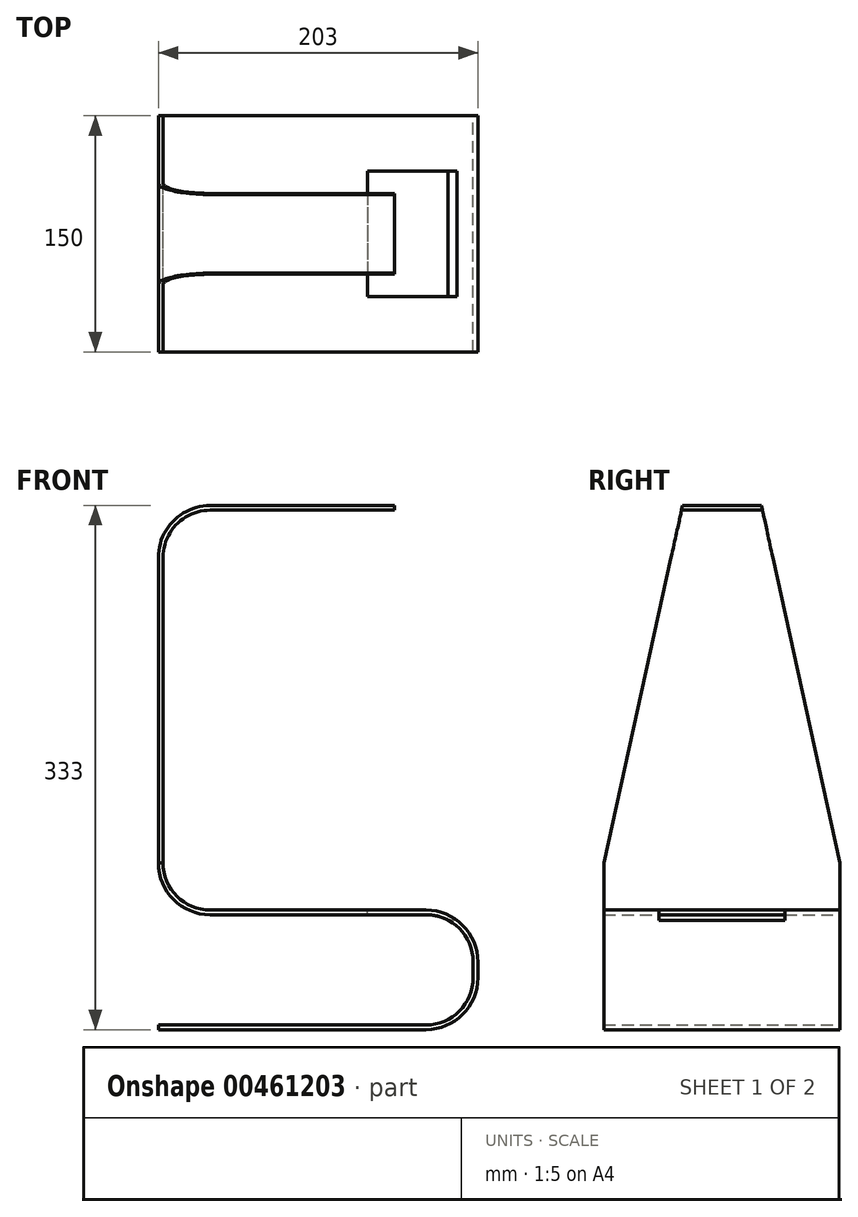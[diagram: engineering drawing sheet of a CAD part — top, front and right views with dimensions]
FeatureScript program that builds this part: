
annotation { "Feature Type Name" : "Feature", "Feature Type Description" : "" }
export const myFeature = defineFeature(function(context is Context, id is Id, definition is map)
    precondition{}
    {
        {
            var Q0;
            Q0=qCreatedBy(makeId("Front.planeOp"),FACE);
            var sketch = newSketch(context, id + "F0", { "sketchPlane" : qUnion([Q0])});
            skLineSegment(sketch, "E0.bottom", {"start": v(70, 35) * mm, "end": v(-67, 35) * mm});
            skLineSegment(sketch, "E0.top", {"start": v(70, -35) * mm, "end": v(-100, -35) * mm});
            skLineSegment(sketch, "E0.left", {"start": v(100, 5) * mm, "end": v(100, -5) * mm});
            skPoint(sketch, "E0.middle", {"position": v(0, 0) * mm});
            skLineSegment(sketch, "E1", {"start": v(-100, 68) * mm, "end": v(-100, 265) * mm});
            skLineSegment(sketch, "E2", {"start": v(-70, 295) * mm, "end": v(50, 295) * mm});
            skPoint(sketch, "E3.visualSharp", {"position": v(-100, 35) * mm});
            skArc(sketch, "E3.filletArc", {"start": v(-100, 68) * mm, "mid": v(-90.33, 44.67) * mm, "end": v(-67, 35) * mm});
            skPoint(sketch, "E4.visualSharp", {"position": v(-100, 295) * mm});
            skPoint(sketch, "E5.visualSharp", {"position": v(100, 35) * mm});
            skArc(sketch, "E5.filletArc", {"start": v(100, 5) * mm, "mid": v(91.21, 26.21) * mm, "end": v(70, 35) * mm});
            skPoint(sketch, "E6.visualSharp", {"position": v(100, -35) * mm});
            skArc(sketch, "E6.filletArc", {"start": v(70, -35) * mm, "mid": v(91.21, -26.21) * mm, "end": v(100, -5) * mm});
            skLineSegment(sketch, "E7.0", {"start": v(-70, 292) * mm, "end": v(50, 292) * mm});
            skLineSegment(sketch, "E7.2", {"start": v(-97, 68) * mm, "end": v(-97, 265) * mm});
            skArc(sketch, "E7.3", {"start": v(-97, 68) * mm, "mid": v(-88.21, 46.79) * mm, "end": v(-67, 38) * mm});
            skLineSegment(sketch, "E7.4", {"start": v(70, 38) * mm, "end": v(-67, 38) * mm});
            skLineSegment(sketch, "E7.5", {"start": v(70, -38) * mm, "end": v(-100, -38) * mm});
            skArc(sketch, "E7.6", {"start": v(70, -38) * mm, "mid": v(93.33, -28.33) * mm, "end": v(103, -5) * mm});
            skLineSegment(sketch, "E7.7", {"start": v(103, 5) * mm, "end": v(103, -5) * mm});
            skArc(sketch, "E7.8", {"start": v(103, 5) * mm, "mid": v(93.33, 28.33) * mm, "end": v(70, 38) * mm});
            skLineSegment(sketch, "E8", {"start": v(50, 295) * mm, "end": v(50, 292) * mm});
            skLineSegment(sketch, "E9", {"start": v(-100, -38) * mm, "end": v(-100, -35) * mm});
            skLineSegment(sketch, "E10", {"start": v(-97, 262) * mm, "end": v(-97, 265) * mm});
            skLineSegment(sketch, "E11", {"start": v(-100, 262) * mm, "end": v(-100, 265) * mm});
            skLineSegment(sketch, "E12", {"start": v(-67, 292) * mm, "end": v(-70, 292) * mm});
            skLineSegment(sketch, "E13", {"start": v(-67, 295) * mm, "end": v(-70, 295) * mm});
            skPoint(sketch, "E14.visualSharp", {"position": v(-97, 292) * mm});
            skArc(sketch, "E14.filletArc", {"start": v(-67, 292) * mm, "mid": v(-88.21, 283.21) * mm, "end": v(-97, 262) * mm});
            skArc(sketch, "E15.filletArc", {"start": v(-67, 295) * mm, "mid": v(-90.33, 285.33) * mm, "end": v(-100, 262) * mm});
            skSolve(sketch);
        }
        {
            var Q0;
            Q0=makeQuery(id+"F0.imprint","IMPRINT",FACE,{"disambiguationData":[TD([[makeQuery(id+"F0.imprint","IMPRINT",EDGE,{"derivedFrom":sQuery(id+"F0.wireOp",EDGE,"E0.bottom")}),-1.0]])]});
            var Q1;
            {var subQ6=sQuery(id+"F0.wireOp",EDGE,"E2");Q1=makeQuery(id+"F0.imprint","IMPRINT",FACE,{"disambiguationData":[TD([[makeQuery(id+"F0.imprint","IMPRINT",EDGE,{"derivedFrom":subQ6}),-1.0]])]});}
            var Q2;
            {var subQ0=sQuery(id+"F0.wireOp",EDGE,"E13");var subQ1=sQuery(id+"F0.wireOp",EDGE,"E10");var subQ2=makeQuery(id+"F0.imprint","INTERSECT",VERTEX,{"derivedFrom":[subQ1,subQ0]});Q2=makeQuery(id+"F0.imprint","IMPRINT",FACE,{"disambiguationData":[TD([[makeQuery(id+"F0.imprint","IMPRINT",EDGE,{"disambiguationData":[TD([[subQ2,1.0]])],"derivedFrom":subQ1}),1.0]])]});}
            extrude(context, id + "F1", {"entities" : qUnion([Q0, Q1, Q2]), "endBound" : BoundingType.SYMMETRIC, "depth" : 150 * mm});
        }
        {
            var Q0;
            Q0=makeQuery(id+"F1.opExtrude","SWEPT_FACE",FACE,{"disambiguationData":[OSD([sQuery(id+"F0.wireOp",EDGE,"E1")])]});
            var sketch = newSketch(context, id + "F2", { "sketchPlane" : qUnion([Q0])});
            skLineSegment(sketch, "E16", {"start": v(-75, 262) * mm, "end": v(-75, 295) * mm});
            skLineSegment(sketch, "E17", {"start": v(75, 262) * mm, "end": v(75, 295) * mm});
            skLineSegment(sketch, "E18", {"start": v(-75, 295) * mm, "end": v(-25, 295) * mm});
            skLineSegment(sketch, "E19", {"start": v(-25, 295) * mm, "end": v(25, 295) * mm});
            skLineSegment(sketch, "E20", {"start": v(25, 295) * mm, "end": v(75, 295) * mm});
            skLineSegment(sketch, "E21", {"start": v(-25, 295) * mm, "end": v(-75, 68) * mm});
            skLineSegment(sketch, "E22", {"start": v(25, 295) * mm, "end": v(75, 68) * mm});
            skSolve(sketch);
        }
        {
            var Q0;
            Q0 = qSketchRegion(id + "F2", true);
            var Q1;
            {var subQ1=sQuery(id+"F0.wireOp",EDGE,"E1");var subQ2=makeQuery(id+"F1.opExtrude","CAP_EDGE",EDGE,{"disambiguationData":[OSD([subQ1])],"isStart":true});Q1=makeQuery(id+"F2.imprint","IMPRINT",FACE,{"disambiguationData":[TD([[makeQuery(id+"F2.imprint","IMPRINT",EDGE,{"derivedFrom":subQ2}),-1.0]])]});}
            var Q2;
            {var subQ0=sQuery(id+"F2.wireOp",EDGE,"E16");Q2=makeQuery(id+"F2.imprint","IMPRINT",FACE,{"disambiguationData":[TD([[makeQuery(id+"F2.imprint","IMPRINT",EDGE,{"derivedFrom":subQ0}),-1.0]])]});}
            var Q3;
            {var subQ0=sQuery(id+"F2.wireOp",EDGE,"E17");Q3=makeQuery(id+"F2.imprint","IMPRINT",FACE,{"disambiguationData":[TD([[makeQuery(id+"F2.imprint","IMPRINT",EDGE,{"derivedFrom":subQ0}),1.0]])]});}
            var Q4;
            {var subQ1=sQuery(id+"F0.wireOp",EDGE,"E1");var subQ2=makeQuery(id+"F1.opExtrude","CAP_EDGE",EDGE,{"disambiguationData":[OSD([subQ1])],"isStart":false});Q4=makeQuery(id+"F2.imprint","IMPRINT",FACE,{"disambiguationData":[TD([[makeQuery(id+"F2.imprint","IMPRINT",EDGE,{"derivedFrom":subQ2}),1.0]])]});}
            extrude(context, id + "F3", {"entities" : qUnion([Q0, Q1, Q2, Q3, Q4]), "operationType" : NewBodyOperationType.REMOVE, "oppositeDirection" : true, "depth" : 200 * mm});
        }
        {
            var Q0;
            Q0=makeQuery(id+"F1.opExtrude","SWEPT_FACE",FACE,{"disambiguationData":[OSD([sQuery(id+"F0.wireOp",EDGE,"E7.4")])]});
            var sketch = newSketch(context, id + "F4", { "sketchPlane" : qUnion([Q0])});
            skLineSegment(sketch, "E23", {"start": v(0, 0) * mm, "end": v(30, 0) * mm});
            skLineSegment(sketch, "E24", {"start": v(30, 0) * mm, "end": v(103, 0) * mm});
            skLineSegment(sketch, "E25", {"start": v(103, 0) * mm, "end": v(103, 40) * mm});
            skLineSegment(sketch, "E26", {"start": v(103, 0) * mm, "end": v(103, -40) * mm});
            skLineSegment(sketch, "E27", {"start": v(103, -40) * mm, "end": v(33, -40) * mm});
            skLineSegment(sketch, "E28", {"start": v(33, -40) * mm, "end": v(33, 40) * mm});
            skLineSegment(sketch, "E29", {"start": v(33, 40) * mm, "end": v(103, 40) * mm});
            skSolve(sketch);
        }
        {
            var Q0;
            {var subQ0=sQuery(id+"F4.wireOp",EDGE,"E28");var subQ5=sQuery(id+"F4.wireOp",EDGE,"E27");var subQ6=makeQuery(id+"F4.imprint","INTERSECT",VERTEX,{"derivedFrom":[subQ5,subQ0]});Q0=makeQuery(id+"F4.imprint","IMPRINT",FACE,{"disambiguationData":[TD([[makeQuery(id+"F4.imprint","IMPRINT",EDGE,{"disambiguationData":[TD([[subQ6,-1.0]])],"derivedFrom":subQ0}),-1.0]])]});}
            var Q1;
            {var subQ0=sQuery(id+"F4.wireOp",EDGE,"E26");Q1=makeQuery(id+"F4.imprint","IMPRINT",FACE,{"disambiguationData":[TD([[makeQuery(id+"F4.imprint","IMPRINT",EDGE,{"derivedFrom":subQ0}),-1.0]])]});}
            var Q2;
            {var subQ0=sQuery(id+"F4.wireOp",EDGE,"E25");Q2=makeQuery(id+"F4.imprint","IMPRINT",FACE,{"disambiguationData":[TD([[makeQuery(id+"F4.imprint","IMPRINT",EDGE,{"derivedFrom":subQ0}),1.0]])]});}
            var Q3;
            {var subQ0=sQuery(id+"F4.wireOp",EDGE,"E28");var subQ5=sQuery(id+"F4.wireOp",EDGE,"E29");var subQ6=makeQuery(id+"F4.imprint","INTERSECT",VERTEX,{"derivedFrom":[subQ0,subQ5]});Q3=makeQuery(id+"F4.imprint","IMPRINT",FACE,{"disambiguationData":[TD([[makeQuery(id+"F4.imprint","IMPRINT",EDGE,{"disambiguationData":[TD([[subQ6,1.0]])],"derivedFrom":subQ0}),-1.0]])]});}
            extrude(context, id + "F5", {"entities" : qUnion([Q0, Q1, Q2, Q3]), "operationType" : NewBodyOperationType.REMOVE, "endBound" : BoundingType.SYMMETRIC, "oppositeDirection" : true, "depth" : 13 * mm, "offsetDistance" : 25 * mm});
        }
    });
